# Revit family: ONRBH -  1-6-Door - All
name_source: partatom
category: Mechanical Equipment
units: mm (PartAtom-declared; Revit-internal decimal feet)

## family parameters
Always vertical = Yes
Cut with Voids When Loaded = No
OmniClass Number = 23.40.40.11.17
OmniClass Title = Refrigerated Cases
Part Type = Normal
Room Calculation Point = No
Round Connector Dimension = Use Radius
Shared = No
Work Plane-Based = Yes

## types (10) — shared parameters
22" Shelf = Yes
Application Discipline = Beverage
BTUH Parallel = 564
Certifications = NSF 7, UL471, CSA
DATE = 12/21/2015
DESIGNERS NAME = SHIDDRAMESH
Default Elevation = 48"
Defrosts Per Day_2 = 4
Description = High Narrow Reach-In Merchandiser
Discharge Air (°F) = 38 °F
Discharge Air Velocity (FPM) = 380 (FPM)
EQUIPMENT DESCRIPTION = High Narrow Reach-In Merchandiser
EQUIPMENT MARK = ONRBH
Evaporator (°F) = 34 °F
Height = 68"
Item Description = High Narrow Reach-In Merchandiser
Keynote = ONRBH
Legend Number = ONRBH
Manufacturer = HILL PHOENIX
Model = ONRBH
PAINTED METAL EXTERIOR = CHARCOAL BROWN
Size of Door = 30"
Superheat Set Point @ Bulb (°F) = 6-8 °F
TRIM = BLACK PAINTED METAL
Timed-Off Defrost Fail-Safe (Min) = 30 (Min)
Timed-Off Defrost Termination Temp_2 = 47 °F
Type of Door Swing = A-Swing
URL = http://www.hillphoenix.com
Vista-C/60 Amps = 1 A
Width = 34 5/8"

## per-type parameters (varying)
| type | 101 Amps | 101 Watts | 20" Shelf | BTUH Conventional | CENTER LINE & DRAIN | Crossfire/Polaris Amps | Crossfire/Polaris Watts | DOOR CONFIGURATION | Eliminaator Amps | Eliminaator Watts | FAN QUANTITY | GE Immersion Amps | GE Immersion Watts | High Efficiency Amps | High Efficiency Watts | How Many Fans Per Case | Length | Number of Doors | Optimax Pro Amps | Optimax Pro Watts | Vista Optimax Pro Amps | Vista Optimax Pro Watts | Vista-C/60 Watts |
| 1-Door- Beverage | 1 A | 134 W | Yes | 597 | 15" | 1 A | 90 W | MASTER DOOR_1 : 30" X 68 3/8" 2 DOOR A SWING (LEFT OPENING) | 1 A | 134 W | 6 | 1 A | 96 W | 1 A | 158 W | 3 | 30" | 6 | 1 A | 115 W | 1 A | 115 W | 159 W |
| 2-Door- Beverage | 0 A | 47 W | No | 597 | 30" | 0 A | 30 W | MASTER DOOR : 30" X 68 3/8" 2 DOOR A SWING (LEFT OPENING) | 0 A | 47 W | 2 | 0 A | 32 W | 0 A | 53 W | 1 | 60" | 2 | 0 A | 39 W | 0 A | 39 W | 68 W |
| 3-Door- Beverage | 1 A | 68 W | Yes | 597 | 45" | 0 A | 45 W | MASTER DOOR : 30" X 68 3/8" 3 DOOR A SWING (LEFT OPENING) | 1 A | 68 W | 3 | 0 A | 48 W | 1 A | 79 W | 2 | 90" | 3 | 0 A | 58 W | 0 A | 58 W | 91 W |
| 4-Door- Beverage | 1 A | 91 W | Yes | 597 | 60" | 1 A | 60 W | MASTER DOOR : 30" X 68 3/8" 4 DOOR A SWING (LEFT OPENING) | 1 A | 91 W | 4 | 1 A | 64 W | 1 A | 106 W | 2 | 120" | 1 | 1 A | 77 W | 1 A | 77 W | 111 W |
| 5-Door- Beverage | 1 A | 111 W | Yes | 44 | 75" | 1 A | 75 W | MASTER DOOR : 30" X 68 3/8" 5 DOOR A SWING (LEFT OPENING) | 1 A | 111 W | 5 | 1 A | 80 W | 1 A | 132 W | 3 | 150" | 5 | 1 A | 96 W | 1 A | 96 W | 134 W |
| 6-Door- Beverage | 1 A | 134 W | Yes | 597 | 90" | 1 A | 90 W | MASTER DOOR : 30" X 68 3/8" 6 DOOR A SWING (LEFT OPENING) | 1 A | 134 W | 6 | 1 A | 96 W | 1 A | 158 W | 3 | 180" | 6 | 1 A | 115 W | 1 A | 115 W | 159 W |
| 4' | 1 A | 134 W | Yes | 597 | 24" | 1 A | 90 W | MASTER DOOR : 4' | 1 A | 134 W | 6 | 1 A | 96 W | 1 A | 158 W | 3 | 48" | 6 | 1 A | 115 W | 1 A | 115 W | 159 W |
| 6' | 1 A | 134 W | Yes | 597 | 36" | 1 A | 90 W | MASTER DOOR : 6' | 1 A | 134 W | 6 | 1 A | 96 W | 1 A | 158 W | 3 | 72" | 6 | 1 A | 115 W | 1 A | 115 W | 159 W |
| 8' | 1 A | 134 W | Yes | 597 | 48" | 1 A | 90 W | MASTER DOOR : 8' | 1 A | 134 W | 6 | 1 A | 96 W | 1 A | 158 W | 3 | 96" | 6 | 1 A | 115 W | 1 A | 115 W | 159 W |
| 12' | 1 A | 134 W | Yes | 597 | 72" | 1 A | 90 W | MASTER DOOR : 12' | 1 A | 134 W | 6 | 1 A | 96 W | 1 A | 158 W | 3 | 144" | 6 | 1 A | 115 W | 1 A | 115 W | 159 W |

## geometry (parser evidence)
native form markers: Blend x8, Sweep x10
no freeform markers — native parametric forms only
